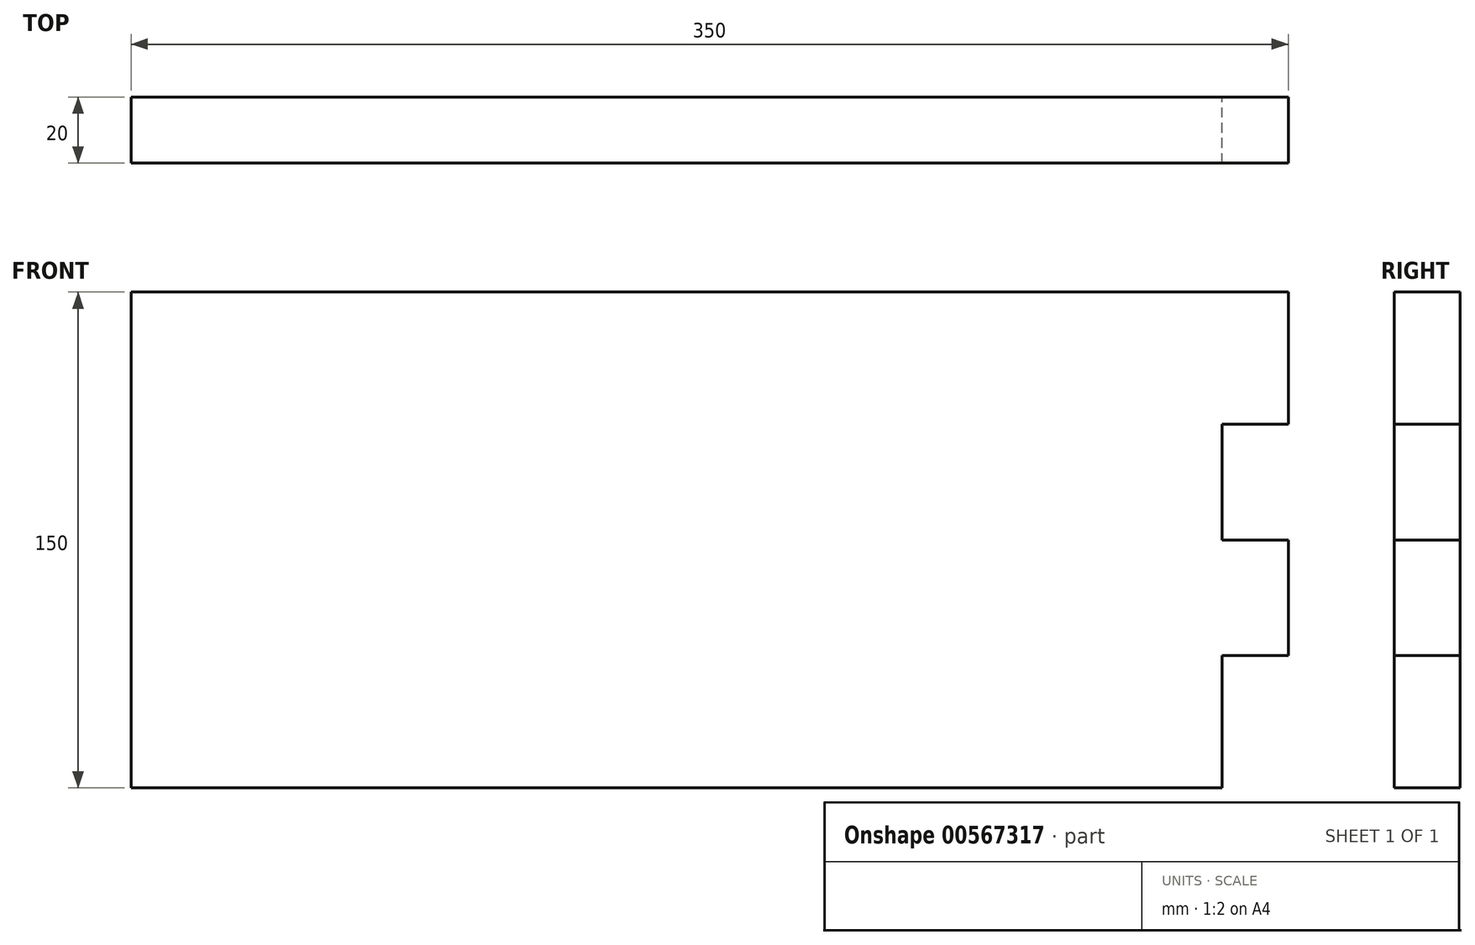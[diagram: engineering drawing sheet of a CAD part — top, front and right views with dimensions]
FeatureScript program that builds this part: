
annotation { "Feature Type Name" : "Feature", "Feature Type Description" : "" }
export const myFeature = defineFeature(function(context is Context, id is Id, definition is map)
    precondition{}
    {
        {
            var Q0;
            Q0=qCreatedBy(makeId("Front.planeOp"),FACE);
            var sketch = newSketch(context, id + "F0", { "sketchPlane" : qUnion([Q0])});
            skLineSegment(sketch, "E0.bottom", {"start": v(-214.42, 109.3) * mm, "end": v(135.58, 109.3) * mm});
            skLineSegment(sketch, "E0.top", {"start": v(-214.42, -40.7) * mm, "end": v(115.58, -40.7) * mm});
            skLineSegment(sketch, "E0.left", {"start": v(-214.42, 109.3) * mm, "end": v(-214.42, -40.7) * mm});
            skLineSegment(sketch, "E0.right", {"start": v(135.58, 109.3) * mm, "end": v(135.58, 69.3) * mm});
            skPoint(sketch, "E1.oppositeSnap0", {"position": v(-214.42, 34.3) * mm});
            skLineSegment(sketch, "E2", {"start": v(115.58, 69.3) * mm, "end": v(115.58, 34.3) * mm});
            skLineSegment(sketch, "E3", {"start": v(115.58, 34.3) * mm, "end": v(135.58, 34.3) * mm});
            skLineSegment(sketch, "E4", {"start": v(115.58, 69.3) * mm, "end": v(135.58, 69.3) * mm});
            skLineSegment(sketch, "E5", {"start": v(115.58, -0.7) * mm, "end": v(135.58, -0.7) * mm});
            skLineSegment(sketch, "E6.trimOffspring", {"start": v(135.58, 34.3) * mm, "end": v(135.58, -0.7) * mm});
            skPoint(sketch, "E7.orphan", {"position": v(115.58, 109.3) * mm});
            skLineSegment(sketch, "E8.trimOffspring", {"start": v(115.58, -0.7) * mm, "end": v(115.58, -40.7) * mm});
            skSolve(sketch);
        }
        {
            var Q0;
            Q0=makeQuery(id+"F0.imprint","IMPRINT",FACE,{"disambiguationData":[TD([[makeQuery(id+"F0.imprint","IMPRINT",EDGE,{"derivedFrom":sQuery(id+"F0.wireOp",EDGE,"E0.bottom")}),-1.0]])]});
            extrude(context, id + "F1", {"entities" : qUnion([Q0]), "depth" : 20 * mm, "offsetDistance" : 25 * mm});
        }
    });
